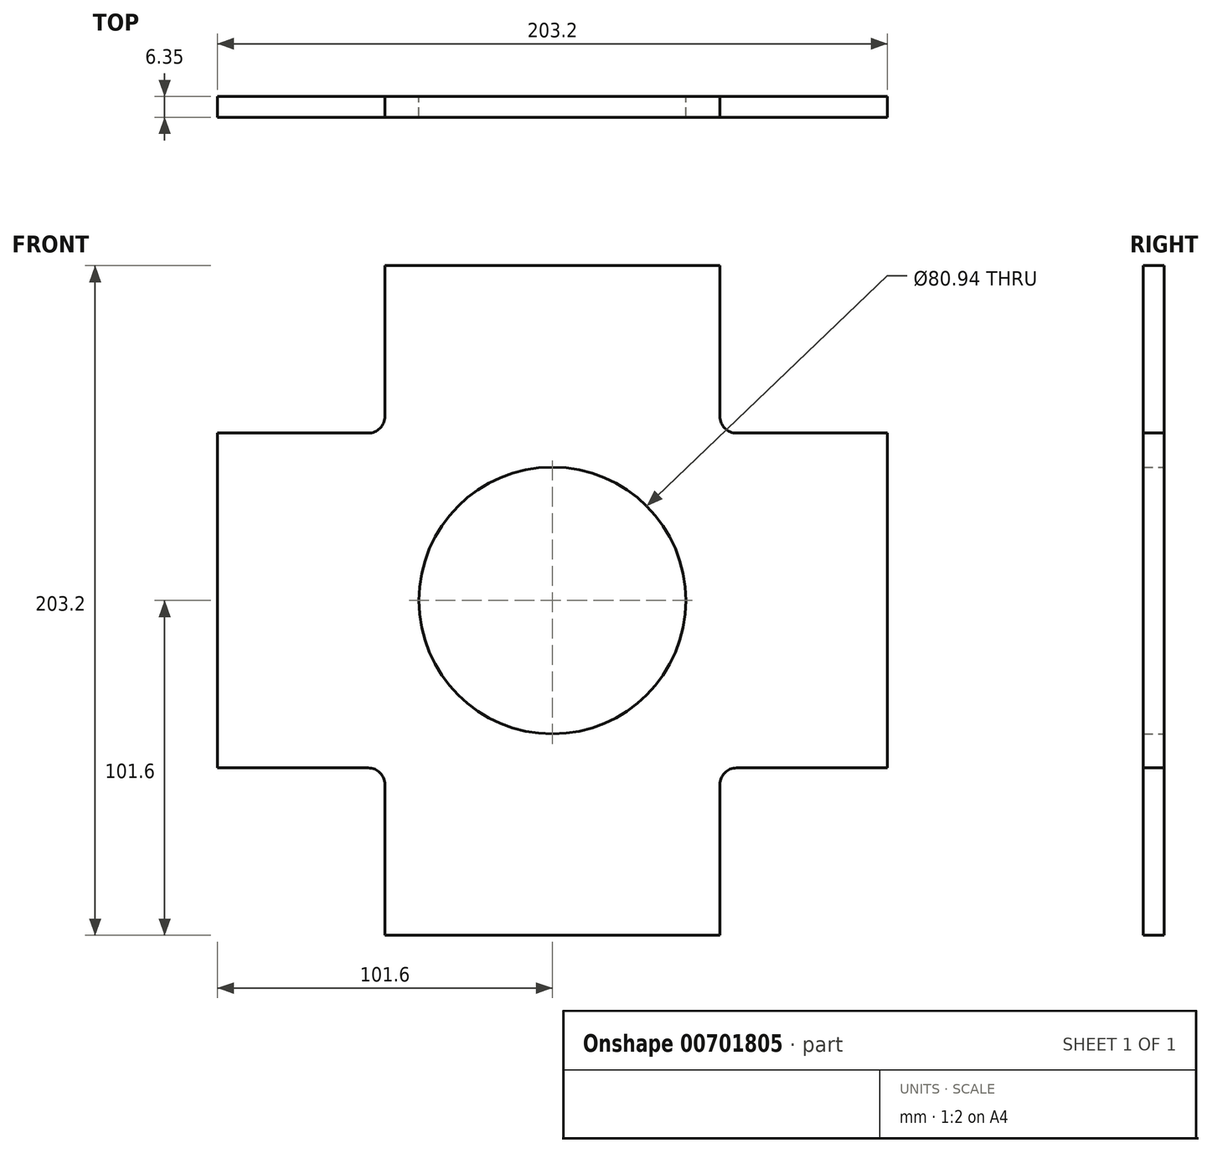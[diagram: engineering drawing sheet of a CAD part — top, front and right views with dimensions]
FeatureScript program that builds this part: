
annotation { "Feature Type Name" : "Feature", "Feature Type Description" : "" }
export const myFeature = defineFeature(function(context is Context, id is Id, definition is map)
    precondition{}
    {
        {
            var Q0;
            Q0=qCreatedBy(makeId("Front.planeOp"),FACE);
            var sketch = newSketch(context, id + "F0", { "sketchPlane" : qUnion([Q0])});
            skLineSegment(sketch, "E0.bottom", {"start": v(50.8, 101.6) * mm, "end": v(-50.8, 101.6) * mm});
            skLineSegment(sketch, "E0.top", {"start": v(50.8, -101.6) * mm, "end": v(-50.8, -101.6) * mm});
            skLineSegment(sketch, "E0.left", {"start": v(101.6, 50.8) * mm, "end": v(101.6, -50.8) * mm});
            skLineSegment(sketch, "E0.right", {"start": v(-101.6, 50.8) * mm, "end": v(-101.6, -50.8) * mm});
            skPoint(sketch, "E0.middle", {"position": v(0, 0) * mm});
            skLineSegment(sketch, "E1", {"start": v(-50.8, 101.6) * mm, "end": v(-50.8, 50.8) * mm});
            skLineSegment(sketch, "E2", {"start": v(50.8, 101.6) * mm, "end": v(50.8, 50.8) * mm});
            skLineSegment(sketch, "E3", {"start": v(-101.6, 50.8) * mm, "end": v(-50.8, 50.8) * mm});
            skLineSegment(sketch, "E4", {"start": v(-101.6, -50.8) * mm, "end": v(-50.8, -50.8) * mm});
            skLineSegment(sketch, "E5.trimOffspring", {"start": v(-50.8, -50.8) * mm, "end": v(-50.8, -101.6) * mm});
            skLineSegment(sketch, "E6.trimOffspring", {"start": v(50.8, 50.8) * mm, "end": v(101.6, 50.8) * mm});
            skLineSegment(sketch, "E7.trimOffspring", {"start": v(50.8, -50.8) * mm, "end": v(50.8, -101.6) * mm});
            skLineSegment(sketch, "E8.trimOffspring", {"start": v(50.8, -50.8) * mm, "end": v(101.6, -50.8) * mm});
            skPoint(sketch, "E9.orphan", {"position": v(101.6, -101.6) * mm});
            skPoint(sketch, "E10.orphan", {"position": v(101.6, 101.6) * mm});
            skPoint(sketch, "E11.orphan", {"position": v(-101.6, 101.6) * mm});
            skPoint(sketch, "E12.orphan", {"position": v(-101.6, -101.6) * mm});
            skCircle(sketch, "E13", {"center": v(0, 0) * mm, "radius": 40.47 * mm});
            skSolve(sketch);
        }
        {
            var Q0;
            Q0=makeQuery(id+"F0.imprint","IMPRINT",FACE,{"disambiguationData":[TD([[makeQuery(id+"F0.imprint","IMPRINT",EDGE,{"derivedFrom":sQuery(id+"F0.wireOp",EDGE,"E0.bottom")}),1.0]])]});
            extrude(context, id + "F1", {"entities" : qUnion([Q0]), "depth" : 6.35 * mm, "offsetDistance" : 25.4 * mm});
        }
        {
            var Q0;
            Q0=makeQuery(id+"F1.opExtrude","SWEPT_EDGE",EDGE,{"disambiguationData":[OSD([sQuery(id+"F0.wireOp",EDGE,"E2"),sQuery(id+"F0.wireOp",EDGE,"E6.trimOffspring")])]});
            var Q1;
            Q1=makeQuery(id+"F1.opExtrude","SWEPT_EDGE",EDGE,{"disambiguationData":[OSD([sQuery(id+"F0.wireOp",EDGE,"E1"),sQuery(id+"F0.wireOp",EDGE,"E3")])]});
            var Q2;
            Q2=makeQuery(id+"F1.opExtrude","SWEPT_EDGE",EDGE,{"disambiguationData":[OSD([sQuery(id+"F0.wireOp",EDGE,"E4"),sQuery(id+"F0.wireOp",EDGE,"E5.trimOffspring")])]});
            var Q3;
            Q3=makeQuery(id+"F1.opExtrude","SWEPT_EDGE",EDGE,{"disambiguationData":[OSD([sQuery(id+"F0.wireOp",EDGE,"E7.trimOffspring"),sQuery(id+"F0.wireOp",EDGE,"E8.trimOffspring")])]});
            fillet(context, id + "F2", {"entities" : qUnion([Q0, Q1, Q2, Q3]), "radius" : 5.08 * mm, "tangentPropagation" : true, "allowEdgeOverflow" : false});
        }
    });
